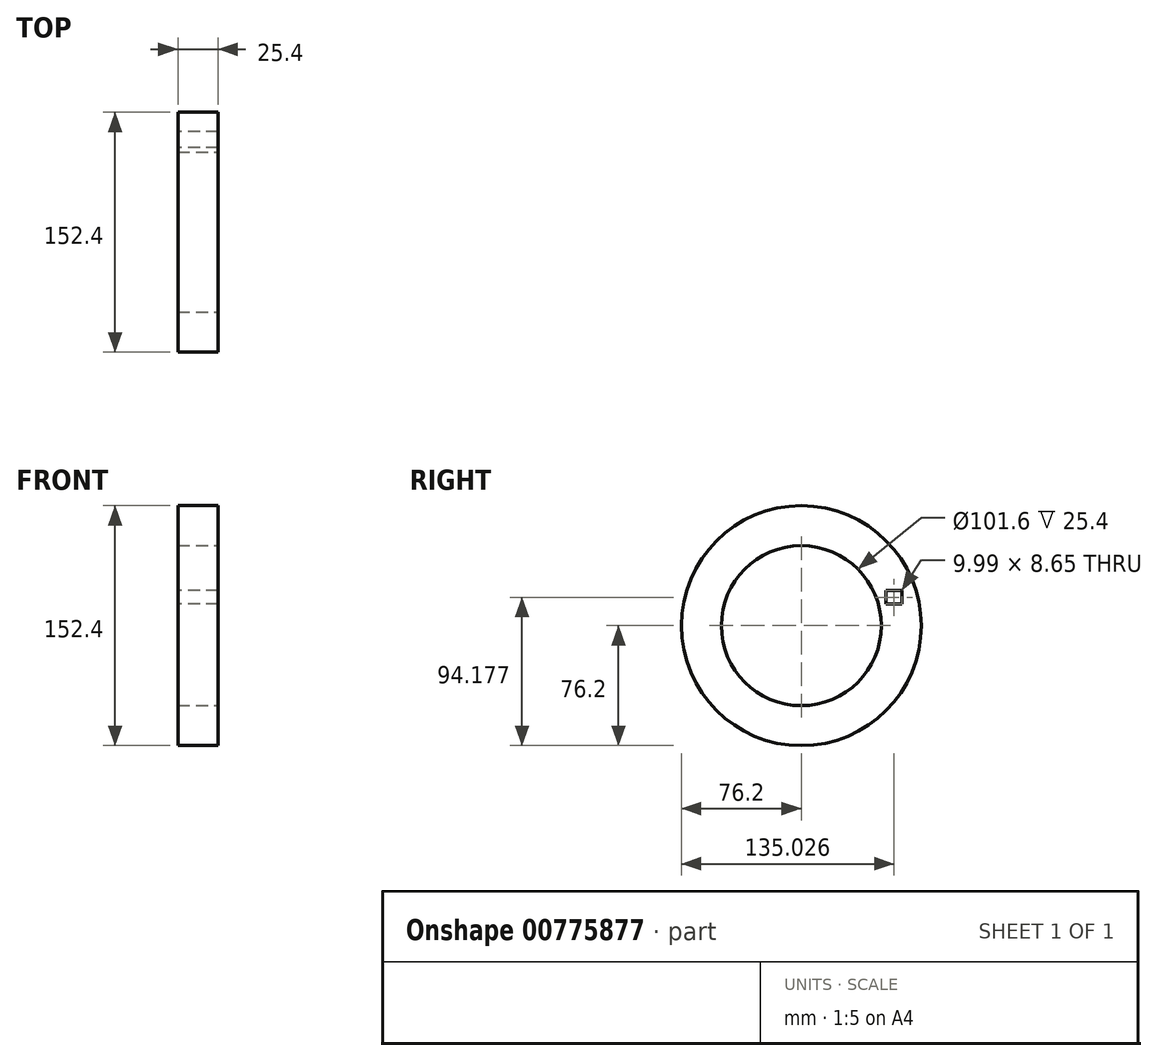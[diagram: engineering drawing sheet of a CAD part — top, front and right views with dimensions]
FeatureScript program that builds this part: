
annotation { "Feature Type Name" : "Feature", "Feature Type Description" : "" }
export const myFeature = defineFeature(function(context is Context, id is Id, definition is map)
    precondition{}
    {
        {
            var Q0;
            Q0=qCreatedBy(makeId("Right.planeOp"),FACE);
            var sketch = newSketch(context, id + "F0", { "sketchPlane" : qUnion([Q0])});
            skCircle(sketch, "E0", {"center": v(0, 0) * mm, "radius": 76.2 * mm});
            skSolve(sketch);
        }
        {
            var Q0;
            Q0 = qSketchRegion(id + "Fw3ArDMNISf44XJ_0", true);
            var Q1;
            Q1=makeQuery(id+"F0.imprint","IMPRINT",FACE,{"disambiguationData":[TD([[makeQuery(id+"F0.imprint","IMPRINT",EDGE,{"derivedFrom":sQuery(id+"F0.wireOp",EDGE,"E0")}),1.0]])]});
            extrude(context, id + "F1", {"entities" : qUnion([Q0, Q1]), "depth" : 25.4 * mm, "offsetDistance" : 25.4 * mm});
        }
        {
            var Q0;
            Q0=makeQuery(id+"F1.opExtrude","CAP_FACE",FACE,{"disambiguationData":[OSD([sQuery(id+"F0.wireOp",EDGE,"E0")])],"isStart":false});
            var sketch = newSketch(context, id + "F2", { "sketchPlane" : qUnion([Q0])});
            skCircle(sketch, "E1", {"center": v(0, 0) * mm, "radius": 50.8 * mm});
            skSolve(sketch);
        }
        {
            var Q0;
            Q0 = qSketchRegion(id + "F2", true);
            var Q1;
            Q1=makeQuery(id+"F2.imprint","IMPRINT",FACE,{"disambiguationData":[TD([[makeQuery(id+"F2.imprint","IMPRINT",EDGE,{"derivedFrom":sQuery(id+"F2.wireOp",EDGE,"E1")}),1.0]])]});
            extrude(context, id + "F3", {"entities" : qUnion([Q0, Q1]), "operationType" : NewBodyOperationType.REMOVE, "oppositeDirection" : true, "depth" : 25.4 * mm, "offsetDistance" : 25.4 * mm});
        }
        {
            var Q0;
            Q0=makeQuery(id+"F1.opExtrude","CAP_FACE",FACE,{"disambiguationData":[OSD([sQuery(id+"F0.wireOp",EDGE,"E0")])],"isStart":true});
            var sketch = newSketch(context, id + "F4", { "sketchPlane" : qUnion([Q0])});
            skLineSegment(sketch, "E2.bottom", {"start": v(-63.82, 13.65) * mm, "end": v(-53.83, 13.65) * mm});
            skLineSegment(sketch, "E2.top", {"start": v(-63.82, 22.3) * mm, "end": v(-53.83, 22.3) * mm});
            skLineSegment(sketch, "E2.left", {"start": v(-63.82, 13.65) * mm, "end": v(-63.82, 22.3) * mm});
            skLineSegment(sketch, "E2.right", {"start": v(-53.83, 13.65) * mm, "end": v(-53.83, 22.3) * mm});
            skSolve(sketch);
        }
        {
            var Q0;
            Q0 = qSketchRegion(id + "F4", true);
            extrude(context, id + "F5", {"entities" : qUnion([Q0]), "operationType" : NewBodyOperationType.REMOVE, "oppositeDirection" : true, "depth" : 25.4 * mm, "offsetDistance" : 25.4 * mm});
        }
    });
